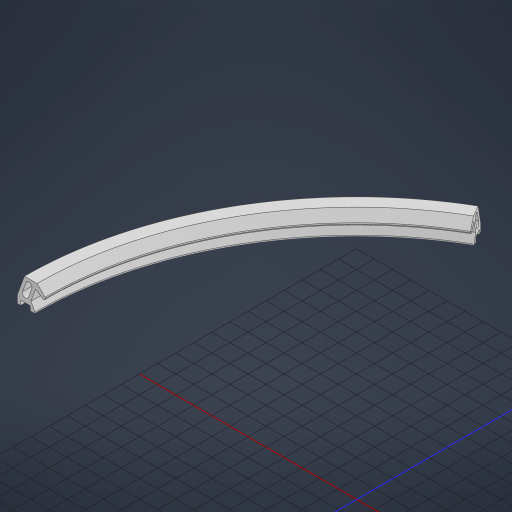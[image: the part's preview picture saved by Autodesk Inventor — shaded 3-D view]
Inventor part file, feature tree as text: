
AUTODESK INVENTOR PART (.ipt)
format: ipt  version: 2023.2 (Build 272271030, 271C)  size: 315,392 bytes
history: native  units: mm
features: revolve x1, sketch x1
ambient origin geometry x8: Origin, YZ Plane, XZ Plane, XY Plane, X Axis, Y Axis, Z Axis, Center Point
bodies: Volumenkörper1 (feature_tree)
feature tree (2):
  revolve  "Umdrehung1"
  sketch  "Skizze1"  dims[d1=30.0mm d5=1.0mm d6=1.0mm d9=135.0deg d14=8.5mm d18=360.0mm d25=50.0mm d26=225.0mm d30=60.0deg d31=14.0mm d40=3.5mm d41=120.0mm d42=35.0mm d43=1.0mm d47=6.0mm d50=11.356478mm d54=15.0mm d55=3.0mm d59=2.094395mm d60=27.925268mm d61=120.0mm d63=3.6mm d64=3.6mm d65=5.0mm d66=15.0mm]
